# Revit family: 756-100-104-DN150-600
name_source: partatom
category: Pipe Accessories
units: mm (PartAtom-declared; Revit-internal decimal feet)

## family parameters
Always vertical = Yes
Cut with Voids When Loaded = No
Part Type = Valve - Breaks Into
Round Connector Dimension = Use Diameter
Shared = No
Work Plane-Based = No

## types (11) — shared parameters
Body_wallthickness = 10 mm  [stored 0.0328084 ft]
DN150 = Yes
DN150_PN10/16 = 756-0150-1-14000
DN200 = Yes
DN200_PN10 = 756-0200-1-04
DN200_PN16 = 756-0200-1-14
DN250 = Yes
DN250_PN10 = 756-0250-1-04
DN250_PN16 = 756-0250-1-14
DN300 = Yes
DN300_PN10 = 756-0300-1-04
DN300_PN16 = 756-0300-1-14
DN350 = Yes
DN350_PN10 = 756-0350-1-04
DN350_PN16 = 756-0350-1-14
DN400 = Yes
DN400_PN10 = 756-0400-1-04
DN400_PN16 = 756-0400-1-14
DN450 = Yes
DN450_PN10 = 756-0450-1-04
DN450_PN16 = 756-0450-1-14
DN500 = Yes
DN500_PN10 = 756-0500-1-04
DN500_PN16 = 756-0500-1-14
DN600 = Yes
DN600_PN10 = 756-0600-1-04
Description_ = AVK_DOUBLE_ECCENTRIC_BUTTERFLY_VALVE
RF_Cut_Thickness = 5 mm  [stored 0.0164042 ft]
Rib_depth = 15 mm  [stored 0.0492126 ft]
Search_table = 756-100-104-DN150-600
URL_product_pages = https://www.avkvalves.com

## per-type parameters (varying)
- DN150_PN10/16: Bottom_Depth=225 mm; Bottom_width=120 mm; C_rod=9 mm  [stored 0.0295276 ft]; D=118 mm; DN=150 mm; DN600_PN16=756-0600-1-14; Disc _width=10 mm  [stored 0.0328084 ft]; Disc_1=2 mm  [stored 0.00656168 ft]; Disc_2=2 mm  [stored 0.00656168 ft]; Disc_Dia=133 mm; Flange_OD=143 mm; Flange_Thickness=15 mm  [stored 0.0492126 ft]; Gear_box_Mount_Flange_thickness=15 mm  [stored 0.0492126 ft]; Gear_box_Mount_Flange_width=68 mm  [stored 0.223097 ft]; Gear_box_Mount_width=43 mm  [stored 0.141076 ft]; Gear_box_width=88 mm; H1=191 mm; H2=201 mm; HW_Connecting_Rib=235 mm; HW_Connecting_Rib_ref=227 mm; HW_Ref=71 mm  [stored 0.23294 ft]; HW_height=269 mm; HW_rod_Dia=15 mm  [stored 0.0492126 ft]; Hand_wheel_rod=37 mm  [stored 0.121391 ft]; ID (Radius)=75 mm  [stored 0.246063 ft]; L=210 mm; L1=1 mm  [stored 0.00328084 ft]; L2=1 mm  [stored 0.00328084 ft]; Offset=3 mm  [stored 0.00984252 ft]; Pin_Depth=218 mm; Pin_dia=30 mm  [stored 0.0984252 ft]; Pin_width=105 mm; Rf_Dia=106 mm; Rib_height=130 mm; Rib_height_2=48 mm  [stored 0.15748 ft]; Rib_width=180 mm; Rib_width_2=136 mm; W1=155 mm; W2=263 mm; W3=6 mm  [stored 0.019685 ft]; W4=6 mm  [stored 0.019685 ft]; W5=276 mm
- DN200_PN10/16: Bottom_Depth=300 mm; Bottom_width=140 mm; C_rod=9 mm  [stored 0.0295276 ft]; D=118 mm; DN=200 mm; DN600_PN16=756-0600-1-14; Disc _width=10 mm  [stored 0.0328084 ft]; Disc_1=2 mm  [stored 0.00656168 ft]; Disc_2=2 mm  [stored 0.00656168 ft]; Disc_Dia=180 mm; Flange_OD=170 mm; Flange_Thickness=15 mm  [stored 0.0492126 ft]; Gear_box_Mount_Flange_thickness=15 mm  [stored 0.0492126 ft]; Gear_box_Mount_Flange_width=68 mm  [stored 0.223097 ft]; Gear_box_Mount_width=43 mm  [stored 0.141076 ft]; Gear_box_width=88 mm; H1=217 mm; H2=227 mm; HW_Connecting_Rib=235 mm; HW_Connecting_Rib_ref=248 mm; HW_Ref=71 mm  [stored 0.23294 ft]; HW_height=269 mm; HW_rod_Dia=15 mm  [stored 0.0492126 ft]; Hand_wheel_rod=32 mm  [stored 0.104987 ft]; ID (Radius)=100 mm; L=230 mm; L1=1 mm  [stored 0.00328084 ft]; L2=1 mm  [stored 0.00328084 ft]; Offset=5 mm  [stored 0.0164042 ft]; Pin_Depth=270 mm; Pin_dia=30 mm  [stored 0.0984252 ft]; Pin_width=115 mm; Rf_Dia=133 mm; Rib_height=155 mm; Rib_height_2=47 mm; Rib_width=200 mm; Rib_width_2=136 mm; W1=182 mm; W2=279 mm; W3=6 mm  [stored 0.019685 ft]; W4=6 mm  [stored 0.019685 ft]; W5=276 mm
- DN250_PN10/16: Bottom_Depth=375 mm; Bottom_width=170 mm; C_rod=14 mm  [stored 0.0459318 ft]; D=118 mm; DN=250 mm; DN600_PN16=756-0600-1-14; Disc _width=15 mm  [stored 0.0492126 ft]; Disc_1=2 mm  [stored 0.00656168 ft]; Disc_2=2 mm  [stored 0.00656168 ft]; Disc_Dia=227 mm; Flange_OD=203 mm; Flange_Thickness=15 mm  [stored 0.0492126 ft]; Gear_box_Mount_Flange_thickness=15 mm  [stored 0.0492126 ft]; Gear_box_Mount_Flange_width=62 mm  [stored 0.203412 ft]; Gear_box_Mount_width=37 mm  [stored 0.121391 ft]; Gear_box_width=81 mm; H1=251 mm; H2=261 mm; HW_Connecting_Rib=235 mm; HW_Connecting_Rib_ref=282 mm; HW_Ref=71 mm  [stored 0.23294 ft]; HW_height=269 mm; HW_rod_Dia=15 mm  [stored 0.0492126 ft]; Hand_wheel_rod=32 mm  [stored 0.104987 ft]; ID (Radius)=125 mm; L=250 mm; L1=1 mm  [stored 0.00328084 ft]; L2=1 mm  [stored 0.00328084 ft]; Offset=5 mm  [stored 0.0164042 ft]; Pin_Depth=328 mm; Pin_dia=30 mm  [stored 0.0984252 ft]; Pin_width=125 mm; Rf_Dia=160 mm; Rib_height=184 mm; Rib_height_2=48 mm  [stored 0.15748 ft]; Rib_width=220 mm; Rib_width_2=124 mm; W1=215 mm; W2=313 mm; W3=6 mm  [stored 0.019685 ft]; W4=6 mm  [stored 0.019685 ft]; W5=276 mm
- DN300_PN10/16: Bottom_Depth=450 mm; Bottom_width=210 mm; C_rod=14 mm  [stored 0.0459318 ft]; D=190 mm; DN=300 mm; DN600_PN16=756-0600-1-14; Disc _width=15 mm  [stored 0.0492126 ft]; Disc_1=3 mm  [stored 0.00984252 ft]; Disc_2=20 mm  [stored 0.0656168 ft]; Disc_Dia=282 mm; Flange_OD=230 mm; Flange_Thickness=20 mm  [stored 0.0656168 ft]; Gear_box_Mount_Flange_thickness=20 mm  [stored 0.0656168 ft]; Gear_box_Mount_Flange_width=75 mm  [stored 0.246063 ft]; Gear_box_Mount_width=45 mm  [stored 0.147638 ft]; Gear_box_width=98 mm; H1=282 mm; H2=292 mm; HW_Connecting_Rib=380 mm; HW_Connecting_Rib_ref=312 mm; HW_Ref=71 mm  [stored 0.23294 ft]; HW_height=296 mm; HW_rod_Dia=20 mm  [stored 0.0656168 ft]; Hand_wheel_rod=31 mm  [stored 0.101706 ft]; ID (Radius)=150 mm; L=270 mm; L1=1 mm  [stored 0.00328084 ft]; L2=12 mm  [stored 0.0393701 ft]; Offset=6 mm  [stored 0.019685 ft]; Pin_Depth=380 mm; Pin_dia=40 mm  [stored 0.131234 ft]; Pin_width=135 mm; Rf_Dia=185 mm; Rib_height=209 mm; Rib_height_2=52 mm; Rib_width=230 mm; Rib_width_2=150 mm; W1=242 mm; W2=343 mm; W3=6 mm  [stored 0.019685 ft]; W4=104 mm; W5=306 mm
- DN350_PN10/16: Bottom_Depth=525 mm; Bottom_width=210 mm; C_rod=19 mm  [stored 0.062336 ft]; D=190 mm; DN=350 mm; DN600_PN16=756-0600-1-14; Disc _width=20 mm  [stored 0.0656168 ft]; Disc_1=20 mm  [stored 0.0656168 ft]; Disc_2=20 mm  [stored 0.0656168 ft]; Disc_Dia=334 mm; Flange_OD=260 mm; Flange_Thickness=20 mm  [stored 0.0656168 ft]; Gear_box_Mount_Flange_thickness=20 mm  [stored 0.0656168 ft]; Gear_box_Mount_Flange_width=80 mm  [stored 0.262467 ft]; Gear_box_Mount_width=50 mm  [stored 0.164042 ft]; Gear_box_width=104 mm; H1=308 mm; H2=318 mm; HW_Connecting_Rib=380 mm; HW_Connecting_Rib_ref=339 mm; HW_Ref=71 mm  [stored 0.23294 ft]; HW_height=296 mm; HW_rod_Dia=20 mm  [stored 0.0656168 ft]; Hand_wheel_rod=31 mm  [stored 0.101706 ft]; ID (Radius)=175 mm; L=290 mm; L1=20 mm  [stored 0.0656168 ft]; L2=26 mm; Offset=3 mm  [stored 0.00984252 ft]; Pin_Depth=435 mm; Pin_dia=40 mm  [stored 0.131234 ft]; Pin_width=145 mm; Rf_Dia=215 mm; Rib_height=236 mm; Rib_height_2=48 mm  [stored 0.15748 ft]; Rib_width=250 mm; Rib_width_2=160 mm; W1=272 mm; W2=369 mm; W3=151 mm; W4=173 mm; W5=306 mm
- DN400_PN10/16: Bottom_Depth=600 mm; Bottom_width=260 mm; C_rod=24 mm  [stored 0.0787402 ft]; D=190 mm; DN=400 mm; DN600_PN16=756-0600-1-14; Disc _width=25 mm  [stored 0.082021 ft]; Disc_1=20 mm  [stored 0.0656168 ft]; Disc_2=20 mm  [stored 0.0656168 ft]; Disc_Dia=383 mm; Flange_OD=290 mm; Flange_Thickness=20 mm  [stored 0.0656168 ft]; Gear_box_Mount_Flange_thickness=20 mm  [stored 0.0656168 ft]; Gear_box_Mount_Flange_width=75 mm  [stored 0.246063 ft]; Gear_box_Mount_width=45 mm  [stored 0.147638 ft]; Gear_box_width=98 mm; H1=339 mm; H2=349 mm; HW_Connecting_Rib=380 mm; HW_Connecting_Rib_ref=371 mm; HW_Ref=80 mm  [stored 0.262467 ft]; HW_height=296 mm; HW_rod_Dia=20 mm  [stored 0.0656168 ft]; Hand_wheel_rod=32 mm  [stored 0.104987 ft]; ID (Radius)=200 mm; L=310 mm; L1=35 mm  [stored 0.114829 ft]; L2=41 mm  [stored 0.134514 ft]; Offset=3 mm  [stored 0.00984252 ft]; Pin_Depth=490 mm; Pin_dia=40 mm  [stored 0.131234 ft]; Pin_width=155 mm; Rf_Dia=240 mm; Rib_height=264 mm; Rib_height_2=49 mm; Rib_width=270 mm; Rib_width_2=150 mm; W1=302 mm; W2=403 mm; W3=215 mm; W4=232 mm; W5=306 mm
- DN450_PN10/16: Bottom_Depth=675 mm; Bottom_width=280 mm; C_rod=24 mm  [stored 0.0787402 ft]; D=235 mm; DN=450 mm; DN600_PN16=756-0600-1-14; Disc _width=25 mm  [stored 0.082021 ft]; Disc_1=20 mm  [stored 0.0656168 ft]; Disc_2=20 mm  [stored 0.0656168 ft]; Disc_Dia=430 mm; Flange_OD=320 mm; Flange_Thickness=30 mm  [stored 0.0984252 ft]; Gear_box_Mount_Flange_thickness=30 mm  [stored 0.0984252 ft]; Gear_box_Mount_Flange_width=93 mm; Gear_box_Mount_width=58 mm  [stored 0.190289 ft]; Gear_box_width=120 mm; H1=360 mm; H2=390 mm; HW_Connecting_Rib=470 mm; HW_Connecting_Rib_ref=400 mm; HW_Ref=86 mm; HW_height=401 mm; HW_rod_Dia=30 mm  [stored 0.0984252 ft]; Hand_wheel_rod=30 mm  [stored 0.0984252 ft]; ID (Radius)=225 mm; L=330 mm; L1=48 mm  [stored 0.15748 ft]; L2=55 mm  [stored 0.180446 ft]; Offset=3 mm  [stored 0.00984252 ft]; Pin_Depth=545 mm; Pin_dia=60 mm  [stored 0.19685 ft]; Pin_width=165 mm; Rf_Dia=265 mm; Rib_height=291 mm; Rib_height_2=40 mm  [stored 0.131234 ft]; Rib_width=270 mm; Rib_width_2=185 mm; W1=332 mm; W2=440 mm; W3=267 mm; W4=284 mm; W5=416 mm
- DN500_PN10: Bottom_Depth=750 mm; Bottom_width=320 mm; C_rod=34 mm; D=185 mm; DN=500 mm; DN600_PN16=756-0600-1-14; Disc _width=35 mm  [stored 0.114829 ft]; Disc_1=20 mm  [stored 0.0656168 ft]; Disc_2=20 mm  [stored 0.0656168 ft]; Disc_Dia=481 mm; Flange_OD=335 mm; Flange_Thickness=30 mm  [stored 0.0984252 ft]; Gear_box_Mount_Flange_thickness=30 mm  [stored 0.0984252 ft]; Gear_box_Mount_Flange_width=93 mm; Gear_box_Mount_width=58 mm  [stored 0.190289 ft]; Gear_box_width=120 mm; H1=390 mm; H2=417 mm; HW_Connecting_Rib=370 mm; HW_Connecting_Rib_ref=434 mm; HW_Ref=86 mm; HW_height=291 mm; HW_rod_Dia=30 mm  [stored 0.0984252 ft]; Hand_wheel_rod=30 mm  [stored 0.0984252 ft]; ID (Radius)=250 mm; L=350 mm; L1=63 mm  [stored 0.206693 ft]; L2=69 mm  [stored 0.226378 ft]; Offset=3 mm  [stored 0.00984252 ft]; Pin_Depth=585 mm; Pin_dia=60 mm  [stored 0.19685 ft]; Pin_width=175 mm; Rf_Dia=291 mm; Rib_height=305 mm; Rib_height_2=55 mm  [stored 0.180446 ft]; Rib_width=290 mm; Rib_width_2=185 mm; W1=338 mm; W2=477 mm; W3=322 mm; W4=335 mm; W5=306 mm
- DN600_PN10: Bottom_Depth=900 mm; Bottom_width=400 mm; C_rod=34 mm; D=285 mm; DN=600 mm; DN600_PN16=756-0600-1-14
756-0600-1-14
756-0600-1-14; Disc _width=35 mm  [stored 0.114829 ft]; Disc_1=20 mm  [stored 0.0656168 ft]; Disc_2=20 mm  [stored 0.0656168 ft]; Disc_Dia=582 mm; Flange_OD=390 mm; Flange_Thickness=30 mm  [stored 0.0984252 ft]; Gear_box_Mount_Flange_thickness=30 mm  [stored 0.0984252 ft]; Gear_box_Mount_Flange_width=103 mm; Gear_box_Mount_width=63 mm  [stored 0.206693 ft]; Gear_box_width=133 mm; H1=465 mm; H2=476 mm; HW_Connecting_Rib=570 mm; HW_Connecting_Rib_ref=506 mm; HW_Ref=104 mm; HW_height=401 mm; HW_rod_Dia=30 mm  [stored 0.0984252 ft]; Hand_wheel_rod=32 mm  [stored 0.104987 ft]; ID (Radius)=300 mm; L=390 mm; L1=94 mm; L2=100 mm; Offset=3 mm  [stored 0.00984252 ft]; Pin_Depth=690 mm; Pin_dia=60 mm  [stored 0.19685 ft]; Pin_width=195 mm; Rf_Dia=341 mm; Rib_height=355 mm; Rib_height_2=75 mm  [stored 0.246063 ft]; Rib_width=330 mm; Rib_width_2=205 mm; W1=393 mm; W2=546 mm; W3=426 mm; W4=437 mm; W5=416 mm
- DN500_PN16: Bottom_Depth=750 mm; Bottom_width=320 mm; C_rod=34 mm; D=235 mm; DN=500 mm; DN600_PN16=756-0600-1-14; Disc _width=35 mm  [stored 0.114829 ft]; Disc_1=20 mm  [stored 0.0656168 ft]; Disc_2=20 mm  [stored 0.0656168 ft]; Disc_Dia=481 mm; Flange_OD=335 mm; Flange_Thickness=30 mm  [stored 0.0984252 ft]; Gear_box_Mount_Flange_thickness=30 mm  [stored 0.0984252 ft]; Gear_box_Mount_Flange_width=93 mm; Gear_box_Mount_width=58 mm  [stored 0.190289 ft]; Gear_box_width=120 mm; H1=390 mm; H2=427 mm; HW_Connecting_Rib=470 mm; HW_Connecting_Rib_ref=443 mm; HW_Ref=86 mm; HW_height=401 mm; HW_rod_Dia=30 mm  [stored 0.0984252 ft]; Hand_wheel_rod=30 mm  [stored 0.0984252 ft]; ID (Radius)=250 mm; L=350 mm; L1=63 mm  [stored 0.206693 ft]; L2=69 mm  [stored 0.226378 ft]; Offset=3 mm  [stored 0.00984252 ft]; Pin_Depth=585 mm; Pin_dia=60 mm  [stored 0.19685 ft]; Pin_width=175 mm; Rf_Dia=291 mm; Rib_height=305 mm; Rib_height_2=55 mm  [stored 0.180446 ft]; Rib_width=290 mm; Rib_width_2=185 mm; W1=370 mm; W2=496 mm; W3=322 mm; W4=335 mm; W5=416 mm
- DN600_PN16: Bottom_Depth=900 mm; Bottom_width=400 mm; C_rod=34 mm; D=285 mm; DN=600 mm; DN600_PN16=756-0600-1-14
756-0600-1-14
756-0600-1-14; Disc _width=35 mm  [stored 0.114829 ft]; Disc_1=20 mm  [stored 0.0656168 ft]; Disc_2=20 mm  [stored 0.0656168 ft]; Disc_Dia=582 mm; Flange_OD=390 mm; Flange_Thickness=30 mm  [stored 0.0984252 ft]; Gear_box_Mount_Flange_thickness=30 mm  [stored 0.0984252 ft]; Gear_box_Mount_Flange_width=103 mm; Gear_box_Mount_width=63 mm  [stored 0.206693 ft]; Gear_box_width=133 mm; H1=465 mm; H2=503 mm; HW_Connecting_Rib=570 mm; HW_Connecting_Rib_ref=526 mm; HW_Ref=104 mm; HW_height=435 mm; HW_rod_Dia=30 mm  [stored 0.0984252 ft]; Hand_wheel_rod=32 mm  [stored 0.104987 ft]; ID (Radius)=300 mm; L=390 mm; L1=94 mm; L2=100 mm; Offset=3 mm  [stored 0.00984252 ft]; Pin_Depth=690 mm; Pin_dia=60 mm  [stored 0.19685 ft]; Pin_width=195 mm; Rf_Dia=341 mm; Rib_height=355 mm; Rib_height_2=75 mm  [stored 0.246063 ft]; Rib_width=330 mm; Rib_width_2=205 mm; W1=435 mm; W2=586 mm; W3=426 mm; W4=437 mm; W5=450 mm

note: [stored X ft] marks values corroborated as IEEE doubles in the binary element streams (Revit-internal decimal feet)

## geometry (parser evidence)
native form markers: Sweep x7
no freeform markers — native parametric forms only
